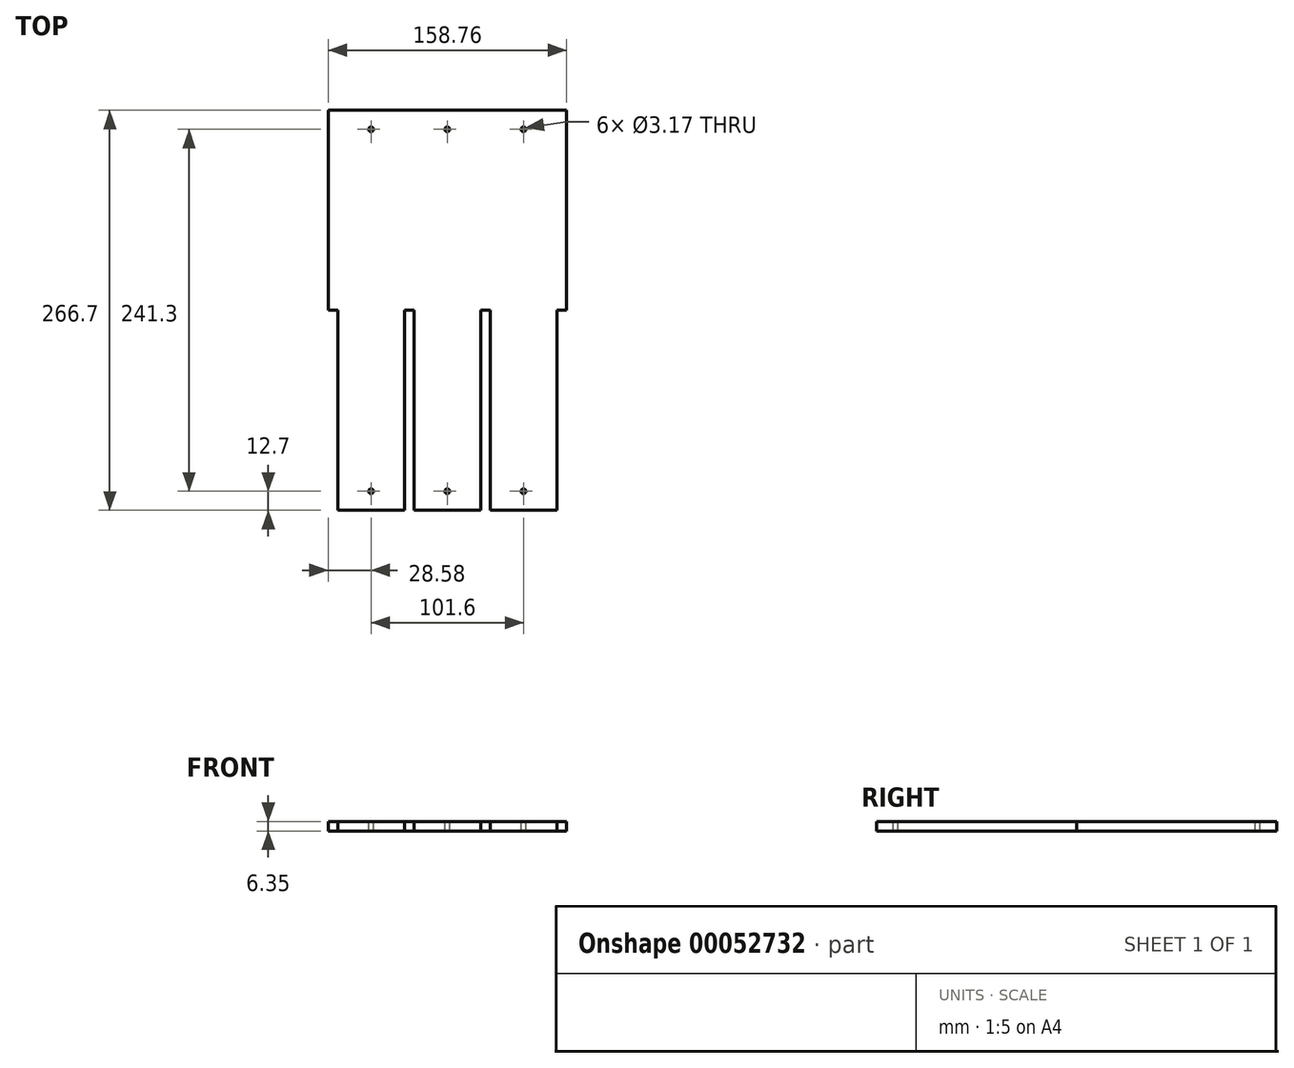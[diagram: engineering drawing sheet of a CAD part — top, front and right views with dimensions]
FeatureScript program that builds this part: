
annotation { "Feature Type Name" : "Feature", "Feature Type Description" : "" }
export const myFeature = defineFeature(function(context is Context, id is Id, definition is map)
    precondition{}
    {
        {
            var Q0;
            Q0=qCreatedBy(makeId("Top.planeOp"),FACE);
            var sketch = newSketch(context, id + "F0", { "sketchPlane" : qUnion([Q0])});
            skLineSegment(sketch, "E0.rect.bottom", {"start": v(-73.02, 133.35) * mm, "end": v(73.03, 133.35) * mm});
            skLineSegment(sketch, "E0.rect.top", {"start": v(-73.03, -133.35) * mm, "end": v(73.02, -133.35) * mm});
            skLineSegment(sketch, "E0.rect.left", {"start": v(-73.02, 133.35) * mm, "end": v(-73.03, -133.35) * mm});
            skLineSegment(sketch, "E0.rect.right", {"start": v(73.03, 133.35) * mm, "end": v(73.02, -133.35) * mm});
            skPoint(sketch, "E0.rect.middle", {"position": v(0, 0) * mm});
            skLineSegment(sketch, "E1.bottom", {"start": v(22.23, 0) * mm, "end": v(28.58, 0) * mm});
            skLineSegment(sketch, "E1.top", {"start": v(22.23, -133.35) * mm, "end": v(28.58, -133.35) * mm});
            skLineSegment(sketch, "E1.left", {"start": v(22.23, 0) * mm, "end": v(22.23, -133.35) * mm});
            skLineSegment(sketch, "E1.right", {"start": v(28.58, 0) * mm, "end": v(28.58, -133.35) * mm});
            skLineSegment(sketch, "E2.bottom", {"start": v(-22.23, 0) * mm, "end": v(-28.58, 0) * mm});
            skLineSegment(sketch, "E2.top", {"start": v(-22.23, -133.35) * mm, "end": v(-28.58, -133.35) * mm});
            skLineSegment(sketch, "E2.left", {"start": v(-22.23, 0) * mm, "end": v(-22.23, -133.35) * mm});
            skLineSegment(sketch, "E2.right", {"start": v(-28.58, 0) * mm, "end": v(-28.58, -133.35) * mm});
            skLineSegment(sketch, "E3", {"start": v(-73.03, -120.65) * mm, "end": v(73.02, -120.65) * mm});
            skLineSegment(sketch, "E4", {"start": v(-73.02, 120.65) * mm, "end": v(73.03, 120.65) * mm});
            skLineSegment(sketch, "E5", {"start": v(-50.8, -120.65) * mm, "end": v(-50.8, 120.65) * mm});
            skLineSegment(sketch, "E6", {"start": v(0, -120.65) * mm, "end": v(0, 120.65) * mm});
            skLineSegment(sketch, "E7", {"start": v(50.8, -120.65) * mm, "end": v(50.8, 120.65) * mm});
            skPoint(sketch, "E8", {"position": v(-50.8, 120.65) * mm});
            skPoint(sketch, "E9", {"position": v(0, 120.65) * mm});
            skPoint(sketch, "E10", {"position": v(50.8, 120.65) * mm});
            skPoint(sketch, "E11", {"position": v(50.8, -120.65) * mm});
            skPoint(sketch, "E12", {"position": v(0, -120.65) * mm});
            skPoint(sketch, "E13", {"position": v(-50.8, -120.65) * mm});
            skPoint(sketch, "E14.firstSnap0", {"position": v(-73.03, 0) * mm});
            skLineSegment(sketch, "E14.bottom", {"start": v(-79.37, 0) * mm, "end": v(79.38, 0) * mm});
            skLineSegment(sketch, "E14.top", {"start": v(-79.37, 133.35) * mm, "end": v(79.37, 133.35) * mm});
            skLineSegment(sketch, "E14.left", {"start": v(-79.37, 0) * mm, "end": v(-79.37, 133.35) * mm});
            skLineSegment(sketch, "E14.right", {"start": v(79.38, 0) * mm, "end": v(79.37, 133.35) * mm});
            skLineSegment(sketch, "E15", {"start": v(-28.58, 0) * mm, "end": v(-28.58, 64.2) * mm});
            skSolve(sketch);
        }
        {
            var Q0;
            {var subQ5=sQuery(id+"F0.wireOp",EDGE,"9bc0c006-8dc3-4b38-ba61-84a232abfa12.rect.left");Q0=makeQuery(id+"F0.imprint","IMPRINT",FACE,{"disambiguationData":[TD([[makeQuery(id+"F0.imprint","IMPRINT",EDGE,{"derivedFrom":subQ5}),1.0]])]});}
            var Q1;
            {var subQ5=sQuery(id+"F0.wireOp",EDGE,"9bc0c006-8dc3-4b38-ba61-84a232abfa12.rect.right");Q1=makeQuery(id+"F0.imprint","IMPRINT",FACE,{"disambiguationData":[TD([[makeQuery(id+"F0.imprint","IMPRINT",EDGE,{"derivedFrom":subQ5}),-1.0]])]});}
            var Q2;
            {var subQ1=sQuery(id+"F0.wireOp",EDGE,"E0.rect.left");var subQ4=sQuery(id+"F0.wireOp",EDGE,"E0.rect.bottom");var subQ5=makeQuery(id+"F0.imprint","INTERSECT",VERTEX,{"derivedFrom":[subQ4,subQ1]});Q2=makeQuery(id+"F0.imprint","IMPRINT",FACE,{"disambiguationData":[TD([[makeQuery(id+"F0.imprint","IMPRINT",EDGE,{"disambiguationData":[TD([[subQ5,-1.0]])],"derivedFrom":subQ4}),-1.0]])]});}
            var Q3;
            {var subQ4=sQuery(id+"F0.wireOp",EDGE,"E0.rect.bottom");var subQ6=sQuery(id+"F0.wireOp",EDGE,"E0.rect.right");var subQ7=makeQuery(id+"F0.imprint","INTERSECT",VERTEX,{"derivedFrom":[subQ4,subQ6]});Q3=makeQuery(id+"F0.imprint","IMPRINT",FACE,{"disambiguationData":[TD([[makeQuery(id+"F0.imprint","IMPRINT",EDGE,{"disambiguationData":[TD([[subQ7,1.0]])],"derivedFrom":subQ4}),-1.0]])]});}
            var Q4;
            {var subQ1=sQuery(id+"F0.wireOp",EDGE,"E0.rect.left");var subQ4=sQuery(id+"F0.wireOp",EDGE,"E0.rect.top");var subQ5=makeQuery(id+"F0.imprint","INTERSECT",VERTEX,{"derivedFrom":[subQ4,subQ1]});Q4=makeQuery(id+"F0.imprint","IMPRINT",FACE,{"disambiguationData":[TD([[makeQuery(id+"F0.imprint","IMPRINT",EDGE,{"disambiguationData":[TD([[subQ5,1.0]])],"derivedFrom":subQ1}),1.0]])]});}
            var Q5;
            {var subQ4=sQuery(id+"F0.wireOp",EDGE,"E0.rect.top");var subQ6=sQuery(id+"F0.wireOp",EDGE,"E0.rect.right");var subQ7=makeQuery(id+"F0.imprint","INTERSECT",VERTEX,{"derivedFrom":[subQ4,subQ6]});Q5=makeQuery(id+"F0.imprint","IMPRINT",FACE,{"disambiguationData":[TD([[makeQuery(id+"F0.imprint","IMPRINT",EDGE,{"disambiguationData":[TD([[subQ7,1.0]])],"derivedFrom":subQ6}),-1.0]])]});}
            var Q6;
            {var subQ0=sQuery(id+"F0.wireOp",EDGE,"E4");var subQ1=sQuery(id+"F0.wireOp",EDGE,"E0.rect.left");var subQ2=makeQuery(id+"F0.imprint","INTERSECT",VERTEX,{"derivedFrom":[subQ1,subQ0]});Q6=makeQuery(id+"F0.imprint","IMPRINT",FACE,{"disambiguationData":[TD([[makeQuery(id+"F0.imprint","IMPRINT",EDGE,{"disambiguationData":[TD([[subQ2,-1.0]])],"derivedFrom":subQ1}),1.0]])]});}
            var Q7;
            {var subQ0=sQuery(id+"F0.wireOp",EDGE,"E3");var subQ1=sQuery(id+"F0.wireOp",EDGE,"E0.rect.left");var subQ2=makeQuery(id+"F0.imprint","INTERSECT",VERTEX,{"derivedFrom":[subQ1,subQ0]});Q7=makeQuery(id+"F0.imprint","IMPRINT",FACE,{"disambiguationData":[TD([[makeQuery(id+"F0.imprint","IMPRINT",EDGE,{"disambiguationData":[TD([[subQ2,1.0]])],"derivedFrom":subQ1}),1.0]])]});}
            var Q8;
            {var subQ0=sQuery(id+"F0.wireOp",EDGE,"E4");var subQ1=sQuery(id+"F0.wireOp",EDGE,"E0.rect.right");var subQ2=makeQuery(id+"F0.imprint","INTERSECT",VERTEX,{"derivedFrom":[subQ1,subQ0]});Q8=makeQuery(id+"F0.imprint","IMPRINT",FACE,{"disambiguationData":[TD([[makeQuery(id+"F0.imprint","IMPRINT",EDGE,{"disambiguationData":[TD([[subQ2,-1.0]])],"derivedFrom":subQ1}),-1.0]])]});}
            var Q9;
            {var subQ0=sQuery(id+"F0.wireOp",EDGE,"E3");var subQ1=sQuery(id+"F0.wireOp",EDGE,"E0.rect.right");var subQ2=makeQuery(id+"F0.imprint","INTERSECT",VERTEX,{"derivedFrom":[subQ1,subQ0]});Q9=makeQuery(id+"F0.imprint","IMPRINT",FACE,{"disambiguationData":[TD([[makeQuery(id+"F0.imprint","IMPRINT",EDGE,{"disambiguationData":[TD([[subQ2,1.0]])],"derivedFrom":subQ1}),-1.0]])]});}
            var Q10;
            {var subQ0=sQuery(id+"F0.wireOp",EDGE,"9bc0c006-8dc3-4b38-ba61-84a232abfa12.rect.bottom");var subQ1=sQuery(id+"F0.wireOp",EDGE,"E0.rect.left");var subQ2=makeQuery(id+"F0.imprint","INTERSECT",VERTEX,{"derivedFrom":[subQ1,subQ0]});Q10=makeQuery(id+"F0.imprint","IMPRINT",FACE,{"disambiguationData":[TD([[makeQuery(id+"F0.imprint","IMPRINT",EDGE,{"disambiguationData":[TD([[subQ2,-1.0]])],"derivedFrom":subQ1}),1.0]])]});}
            var Q11;
            {var subQ0=sQuery(id+"F0.wireOp",EDGE,"9bc0c006-8dc3-4b38-ba61-84a232abfa12.rect.bottom");var subQ1=sQuery(id+"F0.wireOp",EDGE,"E0.rect.right");var subQ2=makeQuery(id+"F0.imprint","INTERSECT",VERTEX,{"derivedFrom":[subQ1,subQ0]});Q11=makeQuery(id+"F0.imprint","IMPRINT",FACE,{"disambiguationData":[TD([[makeQuery(id+"F0.imprint","IMPRINT",EDGE,{"disambiguationData":[TD([[subQ2,-1.0]])],"derivedFrom":subQ1}),-1.0]])]});}
            var Q12;
            {var subQ2=sQuery(id+"F0.wireOp",EDGE,"3e1583db-8840-43eb-9f49-e209081dbd9b.rect.left");var subQ5=sQuery(id+"F0.wireOp",EDGE,"E0.rect.bottom");var subQ8=makeQuery(id+"F0.imprint","INTERSECT",VERTEX,{"derivedFrom":[subQ5,subQ2]});Q12=makeQuery(id+"F0.imprint","IMPRINT",FACE,{"disambiguationData":[TD([[makeQuery(id+"F0.imprint","IMPRINT",EDGE,{"disambiguationData":[TD([[subQ8,-1.0]])],"derivedFrom":subQ5}),-1.0]])]});}
            var Q13;
            {var subQ0=sQuery(id+"F0.wireOp",EDGE,"E5");var subQ1=sQuery(id+"F0.wireOp",EDGE,"9bc0c006-8dc3-4b38-ba61-84a232abfa12.rect.bottom");var subQ2=makeQuery(id+"F0.imprint","INTERSECT",VERTEX,{"derivedFrom":[subQ1,subQ0]});Q13=makeQuery(id+"F0.imprint","IMPRINT",FACE,{"disambiguationData":[TD([[makeQuery(id+"F0.imprint","IMPRINT",EDGE,{"disambiguationData":[TD([[subQ2,-1.0]])],"derivedFrom":subQ1}),1.0]])]});}
            var Q14;
            {var subQ0=sQuery(id+"F0.wireOp",EDGE,"3e1583db-8840-43eb-9f49-e209081dbd9b.rect.left");var subQ1=sQuery(id+"F0.wireOp",EDGE,"9bc0c006-8dc3-4b38-ba61-84a232abfa12.rect.bottom");var subQ2=makeQuery(id+"F0.imprint","INTERSECT",VERTEX,{"derivedFrom":[subQ1,subQ0]});Q14=makeQuery(id+"F0.imprint","IMPRINT",FACE,{"disambiguationData":[TD([[makeQuery(id+"F0.imprint","IMPRINT",EDGE,{"disambiguationData":[TD([[subQ2,-1.0]])],"derivedFrom":subQ1}),1.0]])]});}
            var Q15;
            {var subQ0=sQuery(id+"F0.wireOp",EDGE,"E6");var subQ1=sQuery(id+"F0.wireOp",EDGE,"9bc0c006-8dc3-4b38-ba61-84a232abfa12.rect.bottom");var subQ2=makeQuery(id+"F0.imprint","INTERSECT",VERTEX,{"derivedFrom":[subQ1,subQ0]});Q15=makeQuery(id+"F0.imprint","IMPRINT",FACE,{"disambiguationData":[TD([[makeQuery(id+"F0.imprint","IMPRINT",EDGE,{"disambiguationData":[TD([[subQ2,-1.0]])],"derivedFrom":subQ1}),1.0]])]});}
            var Q16;
            {var subQ0=sQuery(id+"F0.wireOp",EDGE,"3e1583db-8840-43eb-9f49-e209081dbd9b.rect.right");var subQ1=sQuery(id+"F0.wireOp",EDGE,"9bc0c006-8dc3-4b38-ba61-84a232abfa12.rect.bottom");var subQ2=makeQuery(id+"F0.imprint","INTERSECT",VERTEX,{"derivedFrom":[subQ1,subQ0]});Q16=makeQuery(id+"F0.imprint","IMPRINT",FACE,{"disambiguationData":[TD([[makeQuery(id+"F0.imprint","IMPRINT",EDGE,{"disambiguationData":[TD([[subQ2,-1.0]])],"derivedFrom":subQ1}),1.0]])]});}
            var Q17;
            {var subQ0=sQuery(id+"F0.wireOp",EDGE,"E1.bottom");Q17=makeQuery(id+"F0.imprint","IMPRINT",FACE,{"disambiguationData":[TD([[makeQuery(id+"F0.imprint","IMPRINT",EDGE,{"derivedFrom":subQ0}),1.0]])]});}
            var Q18;
            {var subQ0=sQuery(id+"F0.wireOp",EDGE,"E1.right");var subQ1=sQuery(id+"F0.wireOp",EDGE,"9bc0c006-8dc3-4b38-ba61-84a232abfa12.rect.top");var subQ2=makeQuery(id+"F0.imprint","INTERSECT",VERTEX,{"derivedFrom":[subQ1,subQ0]});Q18=makeQuery(id+"F0.imprint","IMPRINT",FACE,{"disambiguationData":[TD([[makeQuery(id+"F0.imprint","IMPRINT",EDGE,{"disambiguationData":[TD([[subQ2,-1.0]])],"derivedFrom":subQ1}),-1.0]])]});}
            var Q19;
            {var subQ0=sQuery(id+"F0.wireOp",EDGE,"E6");var subQ1=sQuery(id+"F0.wireOp",EDGE,"9bc0c006-8dc3-4b38-ba61-84a232abfa12.rect.top");var subQ2=makeQuery(id+"F0.imprint","INTERSECT",VERTEX,{"derivedFrom":[subQ1,subQ0]});Q19=makeQuery(id+"F0.imprint","IMPRINT",FACE,{"disambiguationData":[TD([[makeQuery(id+"F0.imprint","IMPRINT",EDGE,{"disambiguationData":[TD([[subQ2,-1.0]])],"derivedFrom":subQ1}),-1.0]])]});}
            var Q20;
            {var subQ0=sQuery(id+"F0.wireOp",EDGE,"E2.left");var subQ1=sQuery(id+"F0.wireOp",EDGE,"9bc0c006-8dc3-4b38-ba61-84a232abfa12.rect.top");var subQ2=makeQuery(id+"F0.imprint","INTERSECT",VERTEX,{"derivedFrom":[subQ1,subQ0]});Q20=makeQuery(id+"F0.imprint","IMPRINT",FACE,{"disambiguationData":[TD([[makeQuery(id+"F0.imprint","IMPRINT",EDGE,{"disambiguationData":[TD([[subQ2,-1.0]])],"derivedFrom":subQ1}),-1.0]])]});}
            var Q21;
            {var subQ3=sQuery(id+"F0.wireOp",EDGE,"E3");var subQ5=makeQuery(id+"F0.imprint","INTERSECT",VERTEX,{"derivedFrom":[subQ3,sQuery(id+"F0.wireOp",EDGE,"E6")]});Q21=makeQuery(id+"F0.imprint","IMPRINT",FACE,{"disambiguationData":[TD([[makeQuery(id+"F0.imprint","IMPRINT",EDGE,{"disambiguationData":[TD([[subQ5,1.0]])],"derivedFrom":subQ3}),-1.0]])]});}
            var Q22;
            {var subQ0=sQuery(id+"F0.wireOp",EDGE,"E5");var subQ1=sQuery(id+"F0.wireOp",EDGE,"9bc0c006-8dc3-4b38-ba61-84a232abfa12.rect.top");var subQ2=makeQuery(id+"F0.imprint","INTERSECT",VERTEX,{"derivedFrom":[subQ1,subQ0]});Q22=makeQuery(id+"F0.imprint","IMPRINT",FACE,{"disambiguationData":[TD([[makeQuery(id+"F0.imprint","IMPRINT",EDGE,{"disambiguationData":[TD([[subQ2,-1.0]])],"derivedFrom":subQ1}),-1.0]])]});}
            var Q23;
            {var subQ0=sQuery(id+"F0.wireOp",EDGE,"E2.bottom");Q23=makeQuery(id+"F0.imprint","IMPRINT",FACE,{"disambiguationData":[TD([[makeQuery(id+"F0.imprint","IMPRINT",EDGE,{"derivedFrom":subQ0}),-1.0]])]});}
            var Q24;
            {var subQ1=sQuery(id+"F0.wireOp",EDGE,"3e1583db-8840-43eb-9f49-e209081dbd9b.rect.left");var subQ3=sQuery(id+"F0.wireOp",EDGE,"9bc0c006-8dc3-4b38-ba61-84a232abfa12.rect.bottom");var subQ4=makeQuery(id+"F0.imprint","INTERSECT",VERTEX,{"derivedFrom":[subQ3,subQ1]});Q24=makeQuery(id+"F0.imprint","IMPRINT",FACE,{"disambiguationData":[TD([[makeQuery(id+"F0.imprint","IMPRINT",EDGE,{"disambiguationData":[TD([[subQ4,-1.0]])],"derivedFrom":subQ3}),-1.0]])]});}
            var Q25;
            {var subQ3=sQuery(id+"F0.wireOp",EDGE,"9bc0c006-8dc3-4b38-ba61-84a232abfa12.rect.bottom");var subQ5=sQuery(id+"F0.wireOp",EDGE,"E6");var subQ9=makeQuery(id+"F0.imprint","INTERSECT",VERTEX,{"derivedFrom":[subQ3,subQ5]});Q25=makeQuery(id+"F0.imprint","IMPRINT",FACE,{"disambiguationData":[TD([[makeQuery(id+"F0.imprint","IMPRINT",EDGE,{"disambiguationData":[TD([[subQ9,-1.0]])],"derivedFrom":subQ3}),-1.0]])]});}
            var Q26;
            {var subQ0=sQuery(id+"F0.wireOp",EDGE,"E14.bottom");var subQ1=sQuery(id+"F0.wireOp",EDGE,"E2.right");var subQ2=makeQuery(id+"F0.imprint","INTERSECT",VERTEX,{"derivedFrom":[subQ1,subQ0]});Q26=makeQuery(id+"F0.imprint","IMPRINT",FACE,{"disambiguationData":[TD([[makeQuery(id+"F0.imprint","IMPRINT",EDGE,{"disambiguationData":[TD([[subQ2,-1.0]])],"derivedFrom":subQ1}),-1.0]])]});}
            var Q27;
            {var subQ3=sQuery(id+"F0.wireOp",EDGE,"E3");var subQ5=sQuery(id+"F0.wireOp",EDGE,"E6");var subQ6=makeQuery(id+"F0.imprint","INTERSECT",VERTEX,{"derivedFrom":[subQ3,subQ5]});Q27=makeQuery(id+"F0.imprint","IMPRINT",FACE,{"disambiguationData":[TD([[makeQuery(id+"F0.imprint","IMPRINT",EDGE,{"disambiguationData":[TD([[subQ6,1.0]])],"derivedFrom":subQ3}),1.0]])]});}
            var Q28;
            {var subQ3=sQuery(id+"F0.wireOp",EDGE,"E3");var subQ5=sQuery(id+"F0.wireOp",EDGE,"E6");var subQ6=makeQuery(id+"F0.imprint","INTERSECT",VERTEX,{"derivedFrom":[subQ3,subQ5]});Q28=makeQuery(id+"F0.imprint","IMPRINT",FACE,{"disambiguationData":[TD([[makeQuery(id+"F0.imprint","IMPRINT",EDGE,{"disambiguationData":[TD([[subQ6,-1.0]])],"derivedFrom":subQ3}),1.0]])]});}
            var Q29;
            {var subQ0=sQuery(id+"F0.wireOp",EDGE,"E14.bottom");var subQ1=sQuery(id+"F0.wireOp",EDGE,"E1.right");var subQ2=makeQuery(id+"F0.imprint","INTERSECT",VERTEX,{"derivedFrom":[subQ1,subQ0]});Q29=makeQuery(id+"F0.imprint","IMPRINT",FACE,{"disambiguationData":[TD([[makeQuery(id+"F0.imprint","IMPRINT",EDGE,{"disambiguationData":[TD([[subQ2,-1.0]])],"derivedFrom":subQ1}),1.0]])]});}
            var Q30;
            {var subQ0=sQuery(id+"F0.wireOp",EDGE,"E14.right");Q30=makeQuery(id+"F0.imprint","IMPRINT",FACE,{"disambiguationData":[TD([[makeQuery(id+"F0.imprint","IMPRINT",EDGE,{"derivedFrom":subQ0}),1.0]])]});}
            var Q31;
            {var subQ1=sQuery(id+"F0.wireOp",EDGE,"E0.rect.right");var subQ6=sQuery(id+"F0.wireOp",EDGE,"E14.top");var subQ8=makeQuery(id+"F0.imprint","INTERSECT",VERTEX,{"derivedFrom":[subQ1,subQ6]});Q31=makeQuery(id+"F0.imprint","IMPRINT",FACE,{"disambiguationData":[TD([[makeQuery(id+"F0.imprint","IMPRINT",EDGE,{"disambiguationData":[TD([[subQ8,-1.0]])],"derivedFrom":subQ1}),-1.0]])]});}
            var Q32;
            {var subQ4=sQuery(id+"F0.wireOp",EDGE,"E7");var subQ5=sQuery(id+"F0.wireOp",EDGE,"E4");var subQ6=makeQuery(id+"F0.imprint","INTERSECT",VERTEX,{"derivedFrom":[subQ5,subQ4]});Q32=makeQuery(id+"F0.imprint","IMPRINT",FACE,{"disambiguationData":[TD([[makeQuery(id+"F0.imprint","IMPRINT",EDGE,{"disambiguationData":[TD([[subQ6,1.0]])],"derivedFrom":subQ5}),-1.0]])]});}
            var Q33;
            {var subQ3=sQuery(id+"F0.wireOp",EDGE,"E4");var subQ5=sQuery(id+"F0.wireOp",EDGE,"E6");var subQ6=makeQuery(id+"F0.imprint","INTERSECT",VERTEX,{"derivedFrom":[subQ3,subQ5]});Q33=makeQuery(id+"F0.imprint","IMPRINT",FACE,{"disambiguationData":[TD([[makeQuery(id+"F0.imprint","IMPRINT",EDGE,{"disambiguationData":[TD([[subQ6,-1.0]])],"derivedFrom":subQ3}),-1.0]])]});}
            var Q34;
            {var subQ2=sQuery(id+"F0.wireOp",EDGE,"3e1583db-8840-43eb-9f49-e209081dbd9b.rect.left");var subQ4=sQuery(id+"F0.wireOp",EDGE,"E14.top");var subQ8=makeQuery(id+"F0.imprint","INTERSECT",VERTEX,{"derivedFrom":[subQ2,subQ4]});Q34=makeQuery(id+"F0.imprint","IMPRINT",FACE,{"disambiguationData":[TD([[makeQuery(id+"F0.imprint","IMPRINT",EDGE,{"disambiguationData":[TD([[subQ8,-1.0]])],"derivedFrom":subQ2}),1.0]])]});}
            var Q35;
            {var subQ3=sQuery(id+"F0.wireOp",EDGE,"E4");var subQ5=sQuery(id+"F0.wireOp",EDGE,"E6");var subQ6=makeQuery(id+"F0.imprint","INTERSECT",VERTEX,{"derivedFrom":[subQ3,subQ5]});Q35=makeQuery(id+"F0.imprint","IMPRINT",FACE,{"disambiguationData":[TD([[makeQuery(id+"F0.imprint","IMPRINT",EDGE,{"disambiguationData":[TD([[subQ6,1.0]])],"derivedFrom":subQ3}),-1.0]])]});}
            var Q36;
            {var subQ2=sQuery(id+"F0.wireOp",EDGE,"E5");var subQ4=sQuery(id+"F0.wireOp",EDGE,"E4");var subQ5=makeQuery(id+"F0.imprint","INTERSECT",VERTEX,{"derivedFrom":[subQ4,subQ2]});Q36=makeQuery(id+"F0.imprint","IMPRINT",FACE,{"disambiguationData":[TD([[makeQuery(id+"F0.imprint","IMPRINT",EDGE,{"disambiguationData":[TD([[subQ5,-1.0]])],"derivedFrom":subQ4}),-1.0]])]});}
            var Q37;
            {var subQ4=sQuery(id+"F0.wireOp",EDGE,"E14.top");var subQ6=sQuery(id+"F0.wireOp",EDGE,"E0.rect.left");var subQ8=makeQuery(id+"F0.imprint","INTERSECT",VERTEX,{"derivedFrom":[subQ6,subQ4]});Q37=makeQuery(id+"F0.imprint","IMPRINT",FACE,{"disambiguationData":[TD([[makeQuery(id+"F0.imprint","IMPRINT",EDGE,{"disambiguationData":[TD([[subQ8,-1.0]])],"derivedFrom":subQ6}),1.0]])]});}
            var Q38;
            {var subQ3=sQuery(id+"F0.wireOp",EDGE,"E14.left");Q38=makeQuery(id+"F0.imprint","IMPRINT",FACE,{"disambiguationData":[TD([[makeQuery(id+"F0.imprint","IMPRINT",EDGE,{"derivedFrom":subQ3}),-1.0]])]});}
            extrude(context, id + "F1", {"entities" : qUnion([Q0, Q1, Q2, Q3, Q4, Q5, Q6, Q7, Q8, Q9, Q10, Q11, Q12, Q13, Q14, Q15, Q16, Q17, Q18, Q19, Q20, Q21, Q22, Q23, Q24, Q25, Q26, Q27, Q28, Q29, Q30, Q31, Q32, Q33, Q34, Q35, Q36, Q37, Q38]), "depth" : 6.35 * mm});
        }
        {
            var Q0;
            Q0=makeQuery(id+"F1.opExtrude","CAP_FACE",FACE,{"disambiguationData":[OSD([sQuery(id+"F0.wireOp",EDGE,"E0.rect.bottom"),sQuery(id+"F0.wireOp",EDGE,"E0.rect.top"),sQuery(id+"F0.wireOp",EDGE,"E0.rect.left"),sQuery(id+"F0.wireOp",EDGE,"E0.rect.right"),sQuery(id+"F0.wireOp",EDGE,"9bc0c006-8dc3-4b38-ba61-84a232abfa12.rect.bottom"),sQuery(id+"F0.wireOp",EDGE,"9bc0c006-8dc3-4b38-ba61-84a232abfa12.rect.top"),sQuery(id+"F0.wireOp",EDGE,"9bc0c006-8dc3-4b38-ba61-84a232abfa12.rect.left"),sQuery(id+"F0.wireOp",EDGE,"9bc0c006-8dc3-4b38-ba61-84a232abfa12.rect.right"),sQuery(id+"F0.wireOp",EDGE,"3e1583db-8840-43eb-9f49-e209081dbd9b.rect.bottom"),sQuery(id+"F0.wireOp",EDGE,"3e1583db-8840-43eb-9f49-e209081dbd9b.rect.top"),sQuery(id+"F0.wireOp",EDGE,"3e1583db-8840-43eb-9f49-e209081dbd9b.rect.left"),sQuery(id+"F0.wireOp",EDGE,"3e1583db-8840-43eb-9f49-e209081dbd9b.rect.right"),sQuery(id+"F0.wireOp",EDGE,"E1.bottom"),sQuery(id+"F0.wireOp",EDGE,"E1.left"),sQuery(id+"F0.wireOp",EDGE,"E1.right"),sQuery(id+"F0.wireOp",EDGE,"E2.bottom"),sQuery(id+"F0.wireOp",EDGE,"E2.left"),sQuery(id+"F0.wireOp",EDGE,"E2.right")])],"isStart":false});
            var sketch = newSketch(context, id + "F2", { "sketchPlane" : qUnion([Q0])});
            skLineSegment(sketch, "E16", {"start": v(-50.8, -133.35) * mm, "end": v(-50.8, 133.35) * mm});
            skLineSegment(sketch, "E17", {"start": v(0, -139.7) * mm, "end": v(0, 139.7) * mm});
            skLineSegment(sketch, "E18", {"start": v(50.8, -133.35) * mm, "end": v(50.8, 133.35) * mm});
            skLineSegment(sketch, "E19", {"start": v(-73.03, -120.65) * mm, "end": v(73.02, -120.65) * mm});
            skLineSegment(sketch, "E20", {"start": v(-73.02, 120.65) * mm, "end": v(73.03, 120.65) * mm});
            skPoint(sketch, "E21", {"position": v(-50.8, 120.65) * mm});
            skPoint(sketch, "E22", {"position": v(0, 120.65) * mm});
            skPoint(sketch, "E23", {"position": v(50.8, 120.65) * mm});
            skPoint(sketch, "E24", {"position": v(50.8, -120.65) * mm});
            skPoint(sketch, "E25", {"position": v(0, -120.65) * mm});
            skPoint(sketch, "E26", {"position": v(-50.8, -120.65) * mm});
            skSolve(sketch);
        }
        {
            var Q0;
            Q0=sQuery(id+"F2.wireOp",VERTEX,"E21");
            var Q1;
            Q1=sQuery(id+"F2.wireOp",VERTEX,"E22");
            var Q2;
            Q2=sQuery(id+"F2.wireOp",VERTEX,"E23");
            var Q3;
            Q3=sQuery(id+"F2.wireOp",VERTEX,"E24");
            var Q4;
            Q4=sQuery(id+"F2.wireOp",VERTEX,"E25");
            var Q5;
            Q5=sQuery(id+"F2.wireOp",VERTEX,"E26");
            var Q6;
            Q6=makeQuery(id+"F1.opExtrude","SWEPT_BODY",BODY,{"disambiguationData":[OSD([sQuery(id+"F0.wireOp",EDGE,"E0.rect.bottom"),sQuery(id+"F0.wireOp",EDGE,"E0.rect.top"),sQuery(id+"F0.wireOp",EDGE,"E0.rect.left"),sQuery(id+"F0.wireOp",EDGE,"E0.rect.right"),sQuery(id+"F0.wireOp",EDGE,"9bc0c006-8dc3-4b38-ba61-84a232abfa12.rect.bottom"),sQuery(id+"F0.wireOp",EDGE,"9bc0c006-8dc3-4b38-ba61-84a232abfa12.rect.top"),sQuery(id+"F0.wireOp",EDGE,"9bc0c006-8dc3-4b38-ba61-84a232abfa12.rect.left"),sQuery(id+"F0.wireOp",EDGE,"9bc0c006-8dc3-4b38-ba61-84a232abfa12.rect.right"),sQuery(id+"F0.wireOp",EDGE,"3e1583db-8840-43eb-9f49-e209081dbd9b.rect.bottom"),sQuery(id+"F0.wireOp",EDGE,"3e1583db-8840-43eb-9f49-e209081dbd9b.rect.top"),sQuery(id+"F0.wireOp",EDGE,"3e1583db-8840-43eb-9f49-e209081dbd9b.rect.left"),sQuery(id+"F0.wireOp",EDGE,"3e1583db-8840-43eb-9f49-e209081dbd9b.rect.right"),sQuery(id+"F0.wireOp",EDGE,"E1.bottom"),sQuery(id+"F0.wireOp",EDGE,"E1.left"),sQuery(id+"F0.wireOp",EDGE,"E1.right"),sQuery(id+"F0.wireOp",EDGE,"E2.bottom"),sQuery(id+"F0.wireOp",EDGE,"E2.left"),sQuery(id+"F0.wireOp",EDGE,"E2.right")])]});
            hole(context, id + "F3", {"style" : HoleStyle.SIMPLE, "holeDiameter" : 3.17 * mm, "endStyle" : HoleEndStyle.THROUGH, "locations" : qUnion([Q0, Q1, Q2, Q3, Q4, Q5]), "scope" : qUnion([Q6])});
        }
    });
